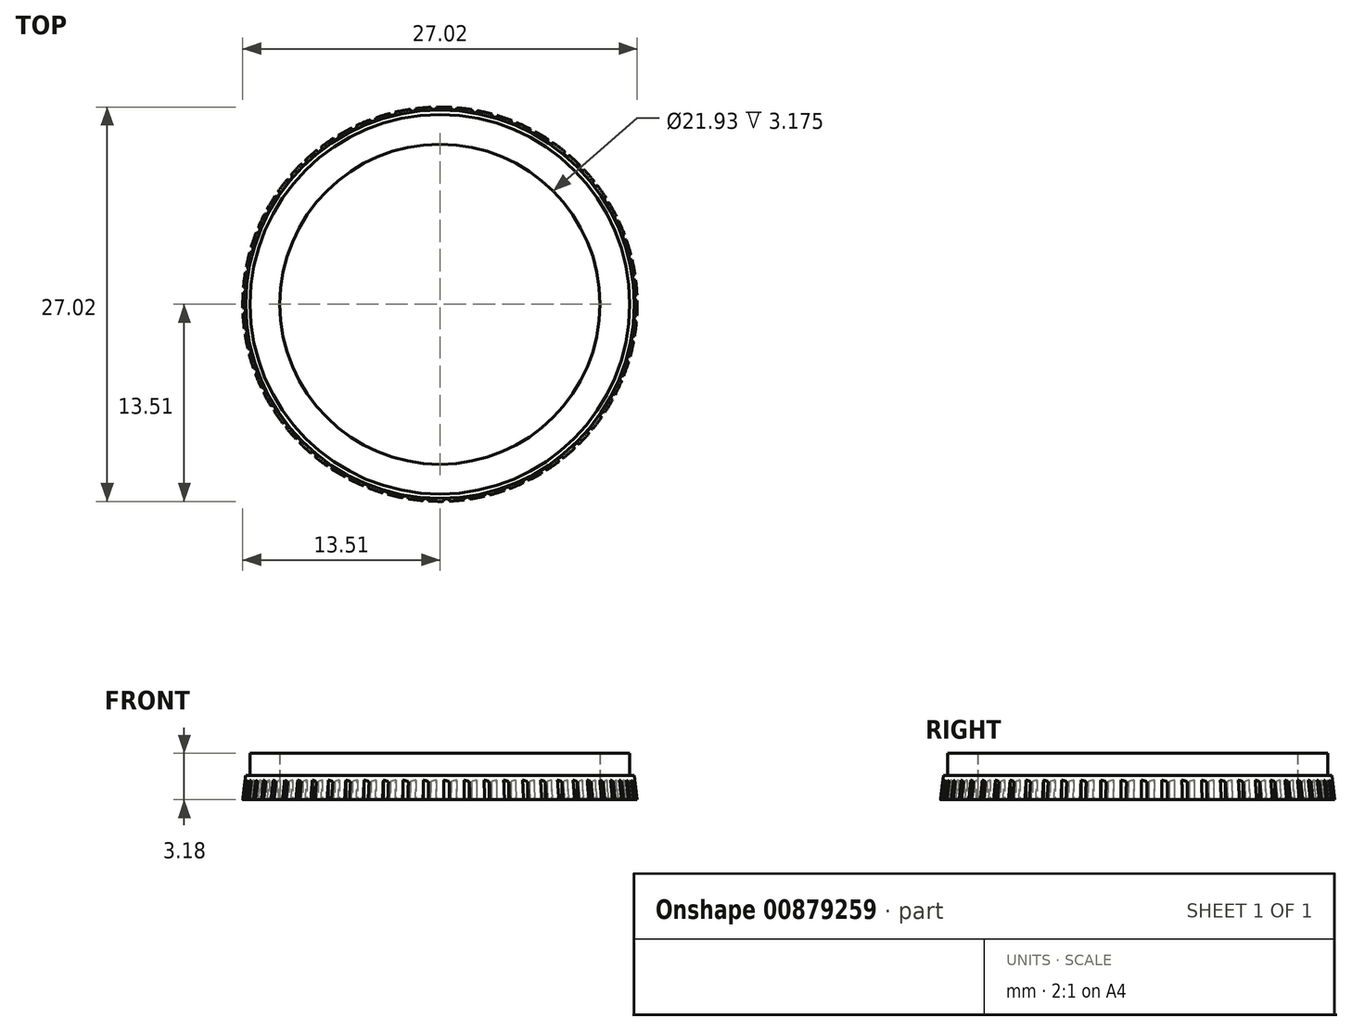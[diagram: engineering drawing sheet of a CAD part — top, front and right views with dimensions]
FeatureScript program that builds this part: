
annotation { "Feature Type Name" : "Feature", "Feature Type Description" : "" }
export const myFeature = defineFeature(function(context is Context, id is Id, definition is map)
    precondition{}
    {
        {
            var Q0;
            Q0=qCreatedBy(makeId("Front.planeOp"),FACE);
            var sketch = newSketch(context, id + "F0", { "sketchPlane" : qUnion([Q0])});
            skLineSegment(sketch, "E0", {"start": v(0, -0.58) * mm, "end": v(0, 5.66) * mm, "construction": true});
            skLineSegment(sketch, "E1", {"start": v(10.97, 0) * mm, "end": v(10.97, 3.18) * mm});
            skLineSegment(sketch, "E2", {"start": v(10.97, 3.18) * mm, "end": v(13, 3.18) * mm});
            skLineSegment(sketch, "E3", {"start": v(13, 3.18) * mm, "end": v(13, 1.66) * mm});
            skLineSegment(sketch, "E4", {"start": v(13, 1.66) * mm, "end": v(13.3, 1.66) * mm});
            skLineSegment(sketch, "E5", {"start": v(13.3, 1.66) * mm, "end": v(13.5, 0) * mm});
            skLineSegment(sketch, "E6", {"start": v(13.5, 0) * mm, "end": v(10.97, 0) * mm});
            skSolve(sketch);
        }
        {
            var Q0;
            Q0 = qSketchRegion(id + "F0", true);
            var Q1;
            Q1=sQuery(id+"F0.wireOp",EDGE,"E0");
            revolve(context, id + "F1", {"surfaceOperationType" : NewSurfaceOperationType.NEW, "entities" : qUnion([Q0]), "axis" : qUnion([Q1]), "revolveType" : RevolveType.FULL});
        }
        {
            var Q0;
            Q0=makeQuery(id+"F1.opRevolve","SWEPT_FACE",FACE,{"disambiguationData":[OSD([sQuery(id+"F0.wireOp",EDGE,"E6")])]});
            var sketch = newSketch(context, id + "F2", { "sketchPlane" : qUnion([Q0])});
            skLineSegment(sketch, "E7.bottom", {"start": v(0.26, 13.55) * mm, "end": v(0.63, 13.55) * mm});
            skLineSegment(sketch, "E7.top", {"start": v(0.26, 13.34) * mm, "end": v(0.63, 13.34) * mm});
            skLineSegment(sketch, "E7.left", {"start": v(0.26, 13.55) * mm, "end": v(0.26, 13.34) * mm});
            skLineSegment(sketch, "E7.right", {"start": v(0.63, 13.55) * mm, "end": v(0.63, 13.34) * mm});
            skLineSegment(sketch, "E8.1.0", {"start": v(-1.16, 13.5) * mm, "end": v(-1.14, 13.3) * mm});
            skLineSegment(sketch, "E8.1.1", {"start": v(-0.8, 13.54) * mm, "end": v(-0.77, 13.33) * mm});
            skLineSegment(sketch, "E8.1.2", {"start": v(-1.14, 13.3) * mm, "end": v(-0.77, 13.33) * mm});
            skLineSegment(sketch, "E8.1.3", {"start": v(-1.16, 13.5) * mm, "end": v(-0.8, 13.54) * mm});
            skLineSegment(sketch, "E8.2.0", {"start": v(-2.57, 13.3) * mm, "end": v(-2.52, 13.1) * mm});
            skLineSegment(sketch, "E8.2.1", {"start": v(-2.2, 13.38) * mm, "end": v(-2.16, 13.18) * mm});
            skLineSegment(sketch, "E8.2.2", {"start": v(-2.52, 13.1) * mm, "end": v(-2.16, 13.18) * mm});
            skLineSegment(sketch, "E8.2.3", {"start": v(-2.57, 13.3) * mm, "end": v(-2.2, 13.38) * mm});
            skLineSegment(sketch, "E8.3.0", {"start": v(-3.94, 12.96) * mm, "end": v(-3.88, 12.77) * mm});
            skLineSegment(sketch, "E8.3.1", {"start": v(-3.6, 13.08) * mm, "end": v(-3.53, 12.88) * mm});
            skLineSegment(sketch, "E8.3.2", {"start": v(-3.88, 12.77) * mm, "end": v(-3.53, 12.88) * mm});
            skLineSegment(sketch, "E8.3.3", {"start": v(-3.94, 12.96) * mm, "end": v(-3.6, 13.08) * mm});
            skLineSegment(sketch, "E8.4.0", {"start": v(-5.28, 12.48) * mm, "end": v(-5.2, 12.3) * mm});
            skLineSegment(sketch, "E8.4.1", {"start": v(-4.94, 12.63) * mm, "end": v(-4.85, 12.44) * mm});
            skLineSegment(sketch, "E8.4.2", {"start": v(-5.2, 12.3) * mm, "end": v(-4.85, 12.44) * mm});
            skLineSegment(sketch, "E8.4.3", {"start": v(-5.28, 12.48) * mm, "end": v(-4.94, 12.63) * mm});
            skLineSegment(sketch, "E8.5.0", {"start": v(-6.55, 11.86) * mm, "end": v(-6.45, 11.68) * mm});
            skLineSegment(sketch, "E8.5.1", {"start": v(-6.23, 12.04) * mm, "end": v(-6.13, 11.87) * mm});
            skLineSegment(sketch, "E8.5.2", {"start": v(-6.45, 11.68) * mm, "end": v(-6.13, 11.87) * mm});
            skLineSegment(sketch, "E8.5.3", {"start": v(-6.55, 11.86) * mm, "end": v(-6.23, 12.04) * mm});
            skLineSegment(sketch, "E8.6.0", {"start": v(-7.76, 11.1) * mm, "end": v(-7.64, 10.94) * mm});
            skLineSegment(sketch, "E8.6.1", {"start": v(-7.46, 11.33) * mm, "end": v(-7.34, 11.16) * mm});
            skLineSegment(sketch, "E8.6.2", {"start": v(-7.64, 10.94) * mm, "end": v(-7.34, 11.16) * mm});
            skLineSegment(sketch, "E8.6.3", {"start": v(-7.76, 11.1) * mm, "end": v(-7.46, 11.33) * mm});
            skLineSegment(sketch, "E8.7.0", {"start": v(-8.87, 10.24) * mm, "end": v(-8.74, 10.09) * mm});
            skLineSegment(sketch, "E8.7.1", {"start": v(-8.6, 10.49) * mm, "end": v(-8.46, 10.33) * mm});
            skLineSegment(sketch, "E8.7.2", {"start": v(-8.74, 10.09) * mm, "end": v(-8.46, 10.33) * mm});
            skLineSegment(sketch, "E8.7.3", {"start": v(-8.87, 10.24) * mm, "end": v(-8.6, 10.49) * mm});
            skLineSegment(sketch, "E8.8.0", {"start": v(-9.9, 9.25) * mm, "end": v(-9.74, 9.12) * mm});
            skLineSegment(sketch, "E8.8.1", {"start": v(-9.65, 9.53) * mm, "end": v(-9.5, 9.4) * mm});
            skLineSegment(sketch, "E8.8.2", {"start": v(-9.74, 9.12) * mm, "end": v(-9.5, 9.4) * mm});
            skLineSegment(sketch, "E8.8.3", {"start": v(-9.9, 9.25) * mm, "end": v(-9.65, 9.53) * mm});
            skLineSegment(sketch, "E8.9.0", {"start": v(-10.8, 8.17) * mm, "end": v(-10.64, 8.05) * mm});
            skLineSegment(sketch, "E8.9.1", {"start": v(-10.6, 8.47) * mm, "end": v(-10.43, 8.35) * mm});
            skLineSegment(sketch, "E8.9.2", {"start": v(-10.64, 8.05) * mm, "end": v(-10.43, 8.35) * mm});
            skLineSegment(sketch, "E8.9.3", {"start": v(-10.8, 8.17) * mm, "end": v(-10.6, 8.47) * mm});
            skLineSegment(sketch, "E8.10.0", {"start": v(-11.6, 7) * mm, "end": v(-11.43, 6.9) * mm});
            skLineSegment(sketch, "E8.10.1", {"start": v(-11.42, 7.32) * mm, "end": v(-11.24, 7.21) * mm});
            skLineSegment(sketch, "E8.10.2", {"start": v(-11.43, 6.9) * mm, "end": v(-11.24, 7.21) * mm});
            skLineSegment(sketch, "E8.10.3", {"start": v(-11.6, 7) * mm, "end": v(-11.42, 7.32) * mm});
            skLineSegment(sketch, "E8.11.0", {"start": v(-12.27, 5.74) * mm, "end": v(-12.08, 5.66) * mm});
            skLineSegment(sketch, "E8.11.1", {"start": v(-12.12, 6.08) * mm, "end": v(-11.93, 6) * mm});
            skLineSegment(sketch, "E8.11.2", {"start": v(-12.08, 5.66) * mm, "end": v(-11.93, 6) * mm});
            skLineSegment(sketch, "E8.11.3", {"start": v(-12.27, 5.74) * mm, "end": v(-12.12, 6.08) * mm});
            skLineSegment(sketch, "E8.12.0", {"start": v(-12.8, 4.43) * mm, "end": v(-12.6, 4.37) * mm});
            skLineSegment(sketch, "E8.12.1", {"start": v(-12.69, 4.78) * mm, "end": v(-12.5, 4.72) * mm});
            skLineSegment(sketch, "E8.12.2", {"start": v(-12.6, 4.37) * mm, "end": v(-12.5, 4.72) * mm});
            skLineSegment(sketch, "E8.12.3", {"start": v(-12.8, 4.43) * mm, "end": v(-12.69, 4.78) * mm});
            skLineSegment(sketch, "E8.13.0", {"start": v(-13.2, 3.07) * mm, "end": v(-13, 3.02) * mm});
            skLineSegment(sketch, "E8.13.1", {"start": v(-13.12, 3.43) * mm, "end": v(-12.92, 3.39) * mm});
            skLineSegment(sketch, "E8.13.2", {"start": v(-13, 3.02) * mm, "end": v(-12.92, 3.39) * mm});
            skLineSegment(sketch, "E8.13.3", {"start": v(-13.2, 3.07) * mm, "end": v(-13.12, 3.43) * mm});
            skLineSegment(sketch, "E8.14.0", {"start": v(-13.44, 1.67) * mm, "end": v(-13.24, 1.65) * mm});
            skLineSegment(sketch, "E8.14.1", {"start": v(-13.4, 2.04) * mm, "end": v(-13.2, 2.02) * mm});
            skLineSegment(sketch, "E8.14.2", {"start": v(-13.24, 1.65) * mm, "end": v(-13.2, 2.02) * mm});
            skLineSegment(sketch, "E8.14.3", {"start": v(-13.44, 1.67) * mm, "end": v(-13.4, 2.04) * mm});
            skLineSegment(sketch, "E8.15.0", {"start": v(-13.55, 0.26) * mm, "end": v(-13.34, 0.26) * mm});
            skLineSegment(sketch, "E8.15.1", {"start": v(-13.55, 0.63) * mm, "end": v(-13.34, 0.63) * mm});
            skLineSegment(sketch, "E8.15.2", {"start": v(-13.34, 0.26) * mm, "end": v(-13.34, 0.63) * mm});
            skLineSegment(sketch, "E8.15.3", {"start": v(-13.55, 0.26) * mm, "end": v(-13.55, 0.63) * mm});
            skLineSegment(sketch, "E8.16.0", {"start": v(-13.5, -1.16) * mm, "end": v(-13.3, -1.14) * mm});
            skLineSegment(sketch, "E8.16.1", {"start": v(-13.54, -0.8) * mm, "end": v(-13.33, -0.77) * mm});
            skLineSegment(sketch, "E8.16.2", {"start": v(-13.3, -1.14) * mm, "end": v(-13.33, -0.77) * mm});
            skLineSegment(sketch, "E8.16.3", {"start": v(-13.5, -1.16) * mm, "end": v(-13.54, -0.8) * mm});
            skLineSegment(sketch, "E8.17.0", {"start": v(-13.3, -2.57) * mm, "end": v(-13.1, -2.52) * mm});
            skLineSegment(sketch, "E8.17.1", {"start": v(-13.38, -2.2) * mm, "end": v(-13.18, -2.16) * mm});
            skLineSegment(sketch, "E8.17.2", {"start": v(-13.1, -2.52) * mm, "end": v(-13.18, -2.16) * mm});
            skLineSegment(sketch, "E8.17.3", {"start": v(-13.3, -2.57) * mm, "end": v(-13.38, -2.2) * mm});
            skLineSegment(sketch, "E8.18.0", {"start": v(-12.96, -3.94) * mm, "end": v(-12.77, -3.88) * mm});
            skLineSegment(sketch, "E8.18.1", {"start": v(-13.08, -3.6) * mm, "end": v(-12.88, -3.53) * mm});
            skLineSegment(sketch, "E8.18.2", {"start": v(-12.77, -3.88) * mm, "end": v(-12.88, -3.53) * mm});
            skLineSegment(sketch, "E8.18.3", {"start": v(-12.96, -3.94) * mm, "end": v(-13.08, -3.6) * mm});
            skLineSegment(sketch, "E8.19.0", {"start": v(-12.48, -5.28) * mm, "end": v(-12.3, -5.2) * mm});
            skLineSegment(sketch, "E8.19.1", {"start": v(-12.63, -4.94) * mm, "end": v(-12.44, -4.85) * mm});
            skLineSegment(sketch, "E8.19.2", {"start": v(-12.3, -5.2) * mm, "end": v(-12.44, -4.85) * mm});
            skLineSegment(sketch, "E8.19.3", {"start": v(-12.48, -5.28) * mm, "end": v(-12.63, -4.94) * mm});
            skLineSegment(sketch, "E8.20.0", {"start": v(-11.86, -6.55) * mm, "end": v(-11.68, -6.45) * mm});
            skLineSegment(sketch, "E8.20.1", {"start": v(-12.04, -6.23) * mm, "end": v(-11.87, -6.13) * mm});
            skLineSegment(sketch, "E8.20.2", {"start": v(-11.68, -6.45) * mm, "end": v(-11.87, -6.13) * mm});
            skLineSegment(sketch, "E8.20.3", {"start": v(-11.86, -6.55) * mm, "end": v(-12.04, -6.23) * mm});
            skLineSegment(sketch, "E8.21.0", {"start": v(-11.1, -7.76) * mm, "end": v(-10.94, -7.64) * mm});
            skLineSegment(sketch, "E8.21.1", {"start": v(-11.33, -7.46) * mm, "end": v(-11.16, -7.34) * mm});
            skLineSegment(sketch, "E8.21.2", {"start": v(-10.94, -7.64) * mm, "end": v(-11.16, -7.34) * mm});
            skLineSegment(sketch, "E8.21.3", {"start": v(-11.1, -7.76) * mm, "end": v(-11.33, -7.46) * mm});
            skLineSegment(sketch, "E8.22.0", {"start": v(-10.24, -8.87) * mm, "end": v(-10.09, -8.74) * mm});
            skLineSegment(sketch, "E8.22.1", {"start": v(-10.49, -8.6) * mm, "end": v(-10.33, -8.46) * mm});
            skLineSegment(sketch, "E8.22.2", {"start": v(-10.09, -8.74) * mm, "end": v(-10.33, -8.46) * mm});
            skLineSegment(sketch, "E8.22.3", {"start": v(-10.24, -8.87) * mm, "end": v(-10.49, -8.6) * mm});
            skLineSegment(sketch, "E8.23.0", {"start": v(-9.25, -9.9) * mm, "end": v(-9.12, -9.74) * mm});
            skLineSegment(sketch, "E8.23.1", {"start": v(-9.53, -9.65) * mm, "end": v(-9.4, -9.5) * mm});
            skLineSegment(sketch, "E8.23.2", {"start": v(-9.12, -9.74) * mm, "end": v(-9.4, -9.5) * mm});
            skLineSegment(sketch, "E8.23.3", {"start": v(-9.25, -9.9) * mm, "end": v(-9.53, -9.65) * mm});
            skLineSegment(sketch, "E8.24.0", {"start": v(-8.17, -10.8) * mm, "end": v(-8.05, -10.64) * mm});
            skLineSegment(sketch, "E8.24.1", {"start": v(-8.47, -10.6) * mm, "end": v(-8.35, -10.43) * mm});
            skLineSegment(sketch, "E8.24.2", {"start": v(-8.05, -10.64) * mm, "end": v(-8.35, -10.43) * mm});
            skLineSegment(sketch, "E8.24.3", {"start": v(-8.17, -10.8) * mm, "end": v(-8.47, -10.6) * mm});
            skLineSegment(sketch, "E8.25.0", {"start": v(-7, -11.6) * mm, "end": v(-6.9, -11.43) * mm});
            skLineSegment(sketch, "E8.25.1", {"start": v(-7.32, -11.42) * mm, "end": v(-7.21, -11.24) * mm});
            skLineSegment(sketch, "E8.25.2", {"start": v(-6.9, -11.43) * mm, "end": v(-7.21, -11.24) * mm});
            skLineSegment(sketch, "E8.25.3", {"start": v(-7, -11.6) * mm, "end": v(-7.32, -11.42) * mm});
            skLineSegment(sketch, "E8.26.0", {"start": v(-5.74, -12.27) * mm, "end": v(-5.66, -12.08) * mm});
            skLineSegment(sketch, "E8.26.1", {"start": v(-6.08, -12.12) * mm, "end": v(-6, -11.93) * mm});
            skLineSegment(sketch, "E8.26.2", {"start": v(-5.66, -12.08) * mm, "end": v(-6, -11.93) * mm});
            skLineSegment(sketch, "E8.26.3", {"start": v(-5.74, -12.27) * mm, "end": v(-6.08, -12.12) * mm});
            skLineSegment(sketch, "E8.27.0", {"start": v(-4.43, -12.8) * mm, "end": v(-4.37, -12.6) * mm});
            skLineSegment(sketch, "E8.27.1", {"start": v(-4.78, -12.69) * mm, "end": v(-4.72, -12.5) * mm});
            skLineSegment(sketch, "E8.27.2", {"start": v(-4.37, -12.6) * mm, "end": v(-4.72, -12.5) * mm});
            skLineSegment(sketch, "E8.27.3", {"start": v(-4.43, -12.8) * mm, "end": v(-4.78, -12.69) * mm});
            skLineSegment(sketch, "E8.28.0", {"start": v(-3.07, -13.2) * mm, "end": v(-3.02, -13) * mm});
            skLineSegment(sketch, "E8.28.1", {"start": v(-3.43, -13.12) * mm, "end": v(-3.39, -12.92) * mm});
            skLineSegment(sketch, "E8.28.2", {"start": v(-3.02, -13) * mm, "end": v(-3.39, -12.92) * mm});
            skLineSegment(sketch, "E8.28.3", {"start": v(-3.07, -13.2) * mm, "end": v(-3.43, -13.12) * mm});
            skLineSegment(sketch, "E8.29.0", {"start": v(-1.67, -13.44) * mm, "end": v(-1.65, -13.24) * mm});
            skLineSegment(sketch, "E8.29.1", {"start": v(-2.04, -13.4) * mm, "end": v(-2.02, -13.2) * mm});
            skLineSegment(sketch, "E8.29.2", {"start": v(-1.65, -13.24) * mm, "end": v(-2.02, -13.2) * mm});
            skLineSegment(sketch, "E8.29.3", {"start": v(-1.67, -13.44) * mm, "end": v(-2.04, -13.4) * mm});
            skPoint(sketch, "E8.center", {"position": v(0, 0) * mm});
            skLineSegment(sketch, "E9.2.30.0", {"start": v(-0.26, -13.55) * mm, "end": v(-0.26, -13.34) * mm});
            skLineSegment(sketch, "E9.3.30.0", {"start": v(-0.63, -13.55) * mm, "end": v(-0.63, -13.34) * mm});
            skLineSegment(sketch, "E9.6.30.0", {"start": v(-0.26, -13.34) * mm, "end": v(-0.63, -13.34) * mm});
            skLineSegment(sketch, "E9.9.30.0", {"start": v(-0.26, -13.55) * mm, "end": v(-0.63, -13.55) * mm});
            skLineSegment(sketch, "E9.2.31.0", {"start": v(1.16, -13.5) * mm, "end": v(1.14, -13.3) * mm});
            skLineSegment(sketch, "E9.3.31.0", {"start": v(0.8, -13.54) * mm, "end": v(0.77, -13.33) * mm});
            skLineSegment(sketch, "E9.6.31.0", {"start": v(1.14, -13.3) * mm, "end": v(0.77, -13.33) * mm});
            skLineSegment(sketch, "E9.9.31.0", {"start": v(1.16, -13.5) * mm, "end": v(0.8, -13.54) * mm});
            skLineSegment(sketch, "E9.2.32.0", {"start": v(2.57, -13.3) * mm, "end": v(2.52, -13.1) * mm});
            skLineSegment(sketch, "E9.3.32.0", {"start": v(2.2, -13.38) * mm, "end": v(2.16, -13.18) * mm});
            skLineSegment(sketch, "E9.6.32.0", {"start": v(2.52, -13.1) * mm, "end": v(2.16, -13.18) * mm});
            skLineSegment(sketch, "E9.9.32.0", {"start": v(2.57, -13.3) * mm, "end": v(2.2, -13.38) * mm});
            skLineSegment(sketch, "E9.2.33.0", {"start": v(3.94, -12.96) * mm, "end": v(3.88, -12.77) * mm});
            skLineSegment(sketch, "E9.3.33.0", {"start": v(3.6, -13.08) * mm, "end": v(3.53, -12.88) * mm});
            skLineSegment(sketch, "E9.6.33.0", {"start": v(3.88, -12.77) * mm, "end": v(3.53, -12.88) * mm});
            skLineSegment(sketch, "E9.9.33.0", {"start": v(3.94, -12.96) * mm, "end": v(3.6, -13.08) * mm});
            skLineSegment(sketch, "E9.2.34.0", {"start": v(5.28, -12.48) * mm, "end": v(5.2, -12.3) * mm});
            skLineSegment(sketch, "E9.3.34.0", {"start": v(4.94, -12.63) * mm, "end": v(4.85, -12.44) * mm});
            skLineSegment(sketch, "E9.6.34.0", {"start": v(5.2, -12.3) * mm, "end": v(4.85, -12.44) * mm});
            skLineSegment(sketch, "E9.9.34.0", {"start": v(5.28, -12.48) * mm, "end": v(4.94, -12.63) * mm});
            skLineSegment(sketch, "E9.2.35.0", {"start": v(6.55, -11.86) * mm, "end": v(6.45, -11.68) * mm});
            skLineSegment(sketch, "E9.3.35.0", {"start": v(6.23, -12.04) * mm, "end": v(6.13, -11.87) * mm});
            skLineSegment(sketch, "E9.6.35.0", {"start": v(6.45, -11.68) * mm, "end": v(6.13, -11.87) * mm});
            skLineSegment(sketch, "E9.9.35.0", {"start": v(6.55, -11.86) * mm, "end": v(6.23, -12.04) * mm});
            skLineSegment(sketch, "E9.2.36.0", {"start": v(7.76, -11.1) * mm, "end": v(7.64, -10.94) * mm});
            skLineSegment(sketch, "E9.3.36.0", {"start": v(7.46, -11.33) * mm, "end": v(7.34, -11.16) * mm});
            skLineSegment(sketch, "E9.6.36.0", {"start": v(7.64, -10.94) * mm, "end": v(7.34, -11.16) * mm});
            skLineSegment(sketch, "E9.9.36.0", {"start": v(7.76, -11.1) * mm, "end": v(7.46, -11.33) * mm});
            skLineSegment(sketch, "E9.2.37.0", {"start": v(8.87, -10.24) * mm, "end": v(8.74, -10.09) * mm});
            skLineSegment(sketch, "E9.3.37.0", {"start": v(8.6, -10.49) * mm, "end": v(8.46, -10.33) * mm});
            skLineSegment(sketch, "E9.6.37.0", {"start": v(8.74, -10.09) * mm, "end": v(8.46, -10.33) * mm});
            skLineSegment(sketch, "E9.9.37.0", {"start": v(8.87, -10.24) * mm, "end": v(8.6, -10.49) * mm});
            skLineSegment(sketch, "E9.2.38.0", {"start": v(9.9, -9.25) * mm, "end": v(9.74, -9.12) * mm});
            skLineSegment(sketch, "E9.3.38.0", {"start": v(9.65, -9.53) * mm, "end": v(9.5, -9.4) * mm});
            skLineSegment(sketch, "E9.6.38.0", {"start": v(9.74, -9.12) * mm, "end": v(9.5, -9.4) * mm});
            skLineSegment(sketch, "E9.9.38.0", {"start": v(9.9, -9.25) * mm, "end": v(9.65, -9.53) * mm});
            skLineSegment(sketch, "E9.2.39.0", {"start": v(10.8, -8.17) * mm, "end": v(10.64, -8.05) * mm});
            skLineSegment(sketch, "E9.3.39.0", {"start": v(10.6, -8.47) * mm, "end": v(10.43, -8.35) * mm});
            skLineSegment(sketch, "E9.6.39.0", {"start": v(10.64, -8.05) * mm, "end": v(10.43, -8.35) * mm});
            skLineSegment(sketch, "E9.9.39.0", {"start": v(10.8, -8.17) * mm, "end": v(10.6, -8.47) * mm});
            skLineSegment(sketch, "E9.2.40.0", {"start": v(11.6, -7) * mm, "end": v(11.43, -6.9) * mm});
            skLineSegment(sketch, "E9.3.40.0", {"start": v(11.42, -7.32) * mm, "end": v(11.24, -7.21) * mm});
            skLineSegment(sketch, "E9.6.40.0", {"start": v(11.43, -6.9) * mm, "end": v(11.24, -7.21) * mm});
            skLineSegment(sketch, "E9.9.40.0", {"start": v(11.6, -7) * mm, "end": v(11.42, -7.32) * mm});
            skLineSegment(sketch, "E9.2.41.0", {"start": v(12.27, -5.74) * mm, "end": v(12.08, -5.66) * mm});
            skLineSegment(sketch, "E9.3.41.0", {"start": v(12.12, -6.08) * mm, "end": v(11.93, -6) * mm});
            skLineSegment(sketch, "E9.6.41.0", {"start": v(12.08, -5.66) * mm, "end": v(11.93, -6) * mm});
            skLineSegment(sketch, "E9.9.41.0", {"start": v(12.27, -5.74) * mm, "end": v(12.12, -6.08) * mm});
            skLineSegment(sketch, "E9.2.42.0", {"start": v(12.8, -4.43) * mm, "end": v(12.6, -4.37) * mm});
            skLineSegment(sketch, "E9.3.42.0", {"start": v(12.69, -4.78) * mm, "end": v(12.5, -4.72) * mm});
            skLineSegment(sketch, "E9.6.42.0", {"start": v(12.6, -4.37) * mm, "end": v(12.5, -4.72) * mm});
            skLineSegment(sketch, "E9.9.42.0", {"start": v(12.8, -4.43) * mm, "end": v(12.69, -4.78) * mm});
            skLineSegment(sketch, "E9.2.43.0", {"start": v(13.2, -3.07) * mm, "end": v(13, -3.02) * mm});
            skLineSegment(sketch, "E9.3.43.0", {"start": v(13.12, -3.43) * mm, "end": v(12.92, -3.39) * mm});
            skLineSegment(sketch, "E9.6.43.0", {"start": v(13, -3.02) * mm, "end": v(12.92, -3.39) * mm});
            skLineSegment(sketch, "E9.9.43.0", {"start": v(13.2, -3.07) * mm, "end": v(13.12, -3.43) * mm});
            skLineSegment(sketch, "E9.2.44.0", {"start": v(13.44, -1.67) * mm, "end": v(13.24, -1.65) * mm});
            skLineSegment(sketch, "E9.3.44.0", {"start": v(13.4, -2.04) * mm, "end": v(13.2, -2.02) * mm});
            skLineSegment(sketch, "E9.6.44.0", {"start": v(13.24, -1.65) * mm, "end": v(13.2, -2.02) * mm});
            skLineSegment(sketch, "E9.9.44.0", {"start": v(13.44, -1.67) * mm, "end": v(13.4, -2.04) * mm});
            skLineSegment(sketch, "E9.2.45.0", {"start": v(13.55, -0.26) * mm, "end": v(13.34, -0.26) * mm});
            skLineSegment(sketch, "E9.3.45.0", {"start": v(13.55, -0.63) * mm, "end": v(13.34, -0.63) * mm});
            skLineSegment(sketch, "E9.6.45.0", {"start": v(13.34, -0.26) * mm, "end": v(13.34, -0.63) * mm});
            skLineSegment(sketch, "E9.9.45.0", {"start": v(13.55, -0.26) * mm, "end": v(13.55, -0.63) * mm});
            skLineSegment(sketch, "E9.2.46.0", {"start": v(13.5, 1.16) * mm, "end": v(13.3, 1.14) * mm});
            skLineSegment(sketch, "E9.3.46.0", {"start": v(13.54, 0.8) * mm, "end": v(13.33, 0.77) * mm});
            skLineSegment(sketch, "E9.6.46.0", {"start": v(13.3, 1.14) * mm, "end": v(13.33, 0.77) * mm});
            skLineSegment(sketch, "E9.9.46.0", {"start": v(13.5, 1.16) * mm, "end": v(13.54, 0.8) * mm});
            skLineSegment(sketch, "E9.2.47.0", {"start": v(13.3, 2.57) * mm, "end": v(13.1, 2.52) * mm});
            skLineSegment(sketch, "E9.3.47.0", {"start": v(13.38, 2.2) * mm, "end": v(13.18, 2.16) * mm});
            skLineSegment(sketch, "E9.6.47.0", {"start": v(13.1, 2.52) * mm, "end": v(13.18, 2.16) * mm});
            skLineSegment(sketch, "E9.9.47.0", {"start": v(13.3, 2.57) * mm, "end": v(13.38, 2.2) * mm});
            skLineSegment(sketch, "E9.2.48.0", {"start": v(12.96, 3.94) * mm, "end": v(12.77, 3.88) * mm});
            skLineSegment(sketch, "E9.3.48.0", {"start": v(13.08, 3.6) * mm, "end": v(12.88, 3.53) * mm});
            skLineSegment(sketch, "E9.6.48.0", {"start": v(12.77, 3.88) * mm, "end": v(12.88, 3.53) * mm});
            skLineSegment(sketch, "E9.9.48.0", {"start": v(12.96, 3.94) * mm, "end": v(13.08, 3.6) * mm});
            skLineSegment(sketch, "E9.2.49.0", {"start": v(12.48, 5.28) * mm, "end": v(12.3, 5.2) * mm});
            skLineSegment(sketch, "E9.3.49.0", {"start": v(12.63, 4.94) * mm, "end": v(12.44, 4.85) * mm});
            skLineSegment(sketch, "E9.6.49.0", {"start": v(12.3, 5.2) * mm, "end": v(12.44, 4.85) * mm});
            skLineSegment(sketch, "E9.9.49.0", {"start": v(12.48, 5.28) * mm, "end": v(12.63, 4.94) * mm});
            skLineSegment(sketch, "E9.2.50.0", {"start": v(11.86, 6.55) * mm, "end": v(11.68, 6.45) * mm});
            skLineSegment(sketch, "E9.3.50.0", {"start": v(12.04, 6.23) * mm, "end": v(11.87, 6.13) * mm});
            skLineSegment(sketch, "E9.6.50.0", {"start": v(11.68, 6.45) * mm, "end": v(11.87, 6.13) * mm});
            skLineSegment(sketch, "E9.9.50.0", {"start": v(11.86, 6.55) * mm, "end": v(12.04, 6.23) * mm});
            skLineSegment(sketch, "E9.2.51.0", {"start": v(11.1, 7.76) * mm, "end": v(10.94, 7.64) * mm});
            skLineSegment(sketch, "E9.3.51.0", {"start": v(11.33, 7.46) * mm, "end": v(11.16, 7.34) * mm});
            skLineSegment(sketch, "E9.6.51.0", {"start": v(10.94, 7.64) * mm, "end": v(11.16, 7.34) * mm});
            skLineSegment(sketch, "E9.9.51.0", {"start": v(11.1, 7.76) * mm, "end": v(11.33, 7.46) * mm});
            skLineSegment(sketch, "E9.2.52.0", {"start": v(10.24, 8.87) * mm, "end": v(10.09, 8.74) * mm});
            skLineSegment(sketch, "E9.3.52.0", {"start": v(10.49, 8.6) * mm, "end": v(10.33, 8.46) * mm});
            skLineSegment(sketch, "E9.6.52.0", {"start": v(10.09, 8.74) * mm, "end": v(10.33, 8.46) * mm});
            skLineSegment(sketch, "E9.9.52.0", {"start": v(10.24, 8.87) * mm, "end": v(10.49, 8.6) * mm});
            skLineSegment(sketch, "E9.2.53.0", {"start": v(9.25, 9.9) * mm, "end": v(9.12, 9.74) * mm});
            skLineSegment(sketch, "E9.3.53.0", {"start": v(9.53, 9.65) * mm, "end": v(9.4, 9.5) * mm});
            skLineSegment(sketch, "E9.6.53.0", {"start": v(9.12, 9.74) * mm, "end": v(9.4, 9.5) * mm});
            skLineSegment(sketch, "E9.9.53.0", {"start": v(9.25, 9.9) * mm, "end": v(9.53, 9.65) * mm});
            skLineSegment(sketch, "E9.2.54.0", {"start": v(8.17, 10.8) * mm, "end": v(8.05, 10.64) * mm});
            skLineSegment(sketch, "E9.3.54.0", {"start": v(8.47, 10.6) * mm, "end": v(8.35, 10.43) * mm});
            skLineSegment(sketch, "E9.6.54.0", {"start": v(8.05, 10.64) * mm, "end": v(8.35, 10.43) * mm});
            skLineSegment(sketch, "E9.9.54.0", {"start": v(8.17, 10.8) * mm, "end": v(8.47, 10.6) * mm});
            skLineSegment(sketch, "E9.2.55.0", {"start": v(7, 11.6) * mm, "end": v(6.9, 11.43) * mm});
            skLineSegment(sketch, "E9.3.55.0", {"start": v(7.32, 11.42) * mm, "end": v(7.21, 11.24) * mm});
            skLineSegment(sketch, "E9.6.55.0", {"start": v(6.9, 11.43) * mm, "end": v(7.21, 11.24) * mm});
            skLineSegment(sketch, "E9.9.55.0", {"start": v(7, 11.6) * mm, "end": v(7.32, 11.42) * mm});
            skLineSegment(sketch, "E9.2.56.0", {"start": v(5.74, 12.27) * mm, "end": v(5.66, 12.08) * mm});
            skLineSegment(sketch, "E9.3.56.0", {"start": v(6.08, 12.12) * mm, "end": v(6, 11.93) * mm});
            skLineSegment(sketch, "E9.6.56.0", {"start": v(5.66, 12.08) * mm, "end": v(6, 11.93) * mm});
            skLineSegment(sketch, "E9.9.56.0", {"start": v(5.74, 12.27) * mm, "end": v(6.08, 12.12) * mm});
            skLineSegment(sketch, "E9.2.57.0", {"start": v(4.43, 12.8) * mm, "end": v(4.37, 12.6) * mm});
            skLineSegment(sketch, "E9.3.57.0", {"start": v(4.78, 12.69) * mm, "end": v(4.72, 12.5) * mm});
            skLineSegment(sketch, "E9.6.57.0", {"start": v(4.37, 12.6) * mm, "end": v(4.72, 12.5) * mm});
            skLineSegment(sketch, "E9.9.57.0", {"start": v(4.43, 12.8) * mm, "end": v(4.78, 12.69) * mm});
            skLineSegment(sketch, "E9.2.58.0", {"start": v(3.07, 13.2) * mm, "end": v(3.02, 13) * mm});
            skLineSegment(sketch, "E9.3.58.0", {"start": v(3.43, 13.12) * mm, "end": v(3.39, 12.92) * mm});
            skLineSegment(sketch, "E9.6.58.0", {"start": v(3.02, 13) * mm, "end": v(3.39, 12.92) * mm});
            skLineSegment(sketch, "E9.9.58.0", {"start": v(3.07, 13.2) * mm, "end": v(3.43, 13.12) * mm});
            skLineSegment(sketch, "E9.2.59.0", {"start": v(1.67, 13.44) * mm, "end": v(1.65, 13.24) * mm});
            skLineSegment(sketch, "E9.3.59.0", {"start": v(2.04, 13.4) * mm, "end": v(2.02, 13.2) * mm});
            skLineSegment(sketch, "E9.6.59.0", {"start": v(1.65, 13.24) * mm, "end": v(2.02, 13.2) * mm});
            skLineSegment(sketch, "E9.9.59.0", {"start": v(1.67, 13.44) * mm, "end": v(2.04, 13.4) * mm});
            skSolve(sketch);
        }
        {
            var Q0;
            Q0 = qSketchRegion(id + "F2", true);
            extrude(context, id + "F3", {"entities" : qUnion([Q0]), "operationType" : NewBodyOperationType.REMOVE, "oppositeDirection" : true, "depth" : 25.4 * mm, "offsetDistance" : 25.4 * mm});
        }
    });
